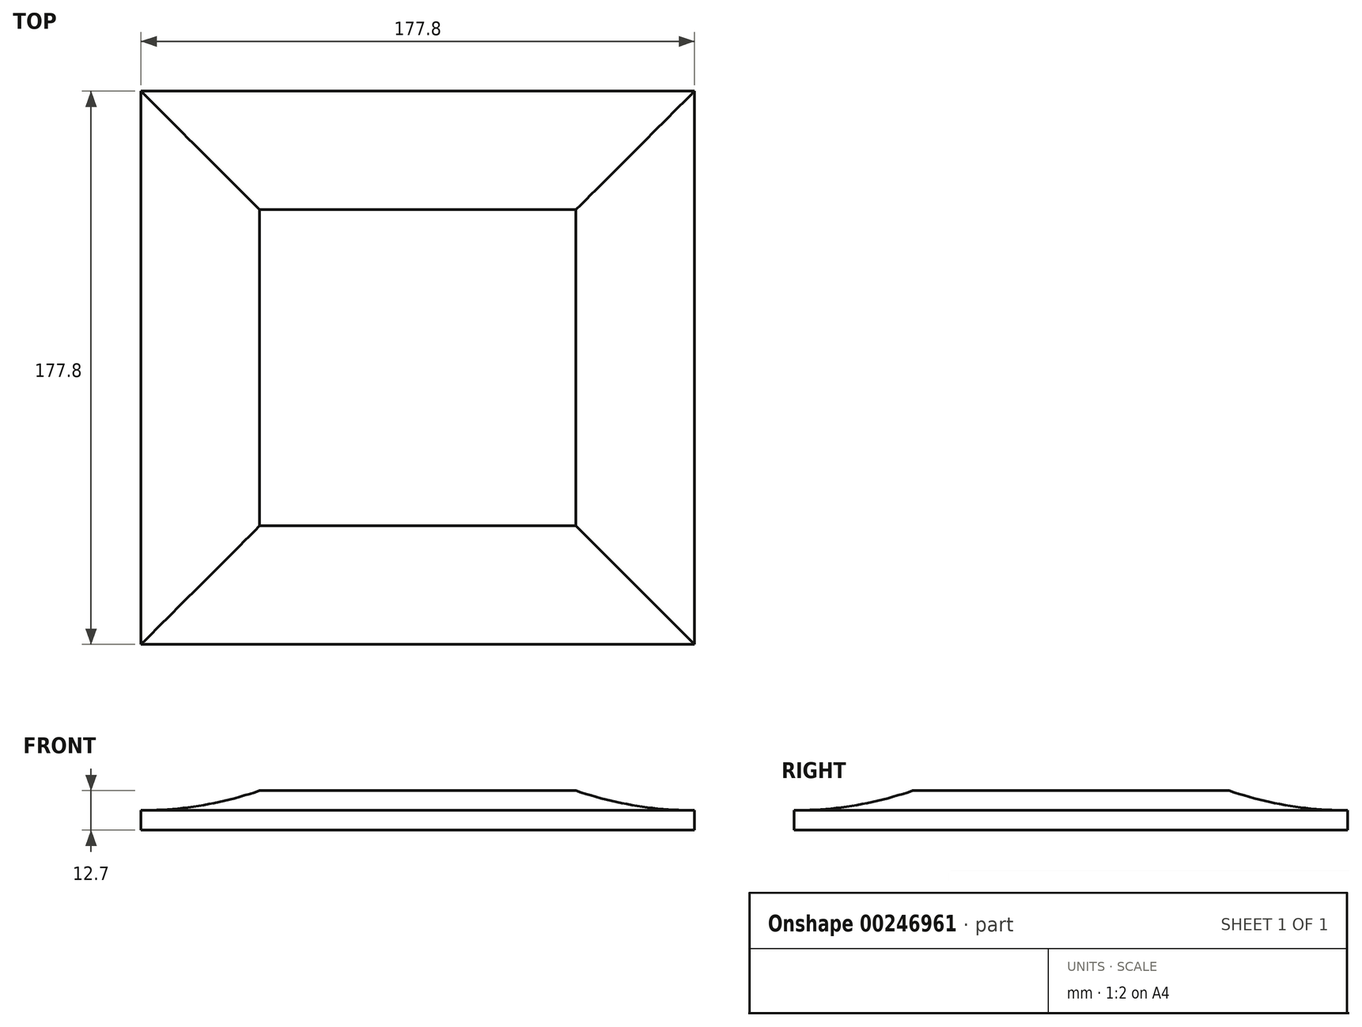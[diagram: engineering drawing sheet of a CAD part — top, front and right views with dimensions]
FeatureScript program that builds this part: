
annotation { "Feature Type Name" : "Feature", "Feature Type Description" : "" }
export const myFeature = defineFeature(function(context is Context, id is Id, definition is map)
    precondition{}
    {
        {
            var Q0;
            Q0=qCreatedBy(makeId("Top.planeOp"),FACE);
            var sketch = newSketch(context, id + "F0", { "sketchPlane" : qUnion([Q0])});
            skLineSegment(sketch, "E0.bottom", {"start": v(88.9, -88.9) * mm, "end": v(-88.9, -88.9) * mm});
            skLineSegment(sketch, "E0.top", {"start": v(88.9, 88.9) * mm, "end": v(-88.9, 88.9) * mm});
            skLineSegment(sketch, "E0.left", {"start": v(88.9, -88.9) * mm, "end": v(88.9, 88.9) * mm});
            skLineSegment(sketch, "E0.right", {"start": v(-88.9, -88.9) * mm, "end": v(-88.9, 88.9) * mm});
            skPoint(sketch, "E0.middle", {"position": v(0, 0) * mm});
            skSolve(sketch);
        }
        {
            var Q0;
            Q0=qCreatedBy(makeId("Front.planeOp"),FACE);
            var sketch = newSketch(context, id + "F1", { "sketchPlane" : qUnion([Q0])});
            skPoint(sketch, "E1.0", {"position": v(88.9, 0) * mm});
            skLineSegment(sketch, "E2", {"start": v(88.9, 0) * mm, "end": v(0, 0) * mm});
            skLineSegment(sketch, "E3", {"start": v(88.9, 0) * mm, "end": v(88.9, 6.35) * mm});
            skLineSegment(sketch, "E4", {"start": v(88.9, 6.35) * mm, "end": v(121.43, 6.35) * mm, "construction": true});
            skLineSegment(sketch, "E5", {"start": v(0, 0) * mm, "end": v(0, 12.7) * mm});
            skLineSegment(sketch, "E6", {"start": v(0, 12.7) * mm, "end": v(50.8, 12.7) * mm});
            skArc(sketch, "E7", {"start": v(88.9, 6.35) * mm, "mid": v(69.59, 7.95) * mm, "end": v(50.8, 12.7) * mm});
            skSolve(sketch);
        }
        {
            var Q0;
            Q0=makeQuery(id+"F1.imprint","IMPRINT",FACE,{"disambiguationData":[TD([[makeQuery(id+"F1.imprint","IMPRINT",EDGE,{"derivedFrom":sQuery(id+"F1.wireOp",EDGE,"E2")}),-1.0]])]});
            var Q1;
            Q1=sQuery(id+"F0.wireOp",EDGE,"E0.left");
            var Q2;
            Q2=sQuery(id+"F0.wireOp",EDGE,"E0.top");
            var Q3;
            Q3=sQuery(id+"F0.wireOp",EDGE,"E0.right");
            var Q4;
            Q4=sQuery(id+"F0.wireOp",EDGE,"E0.bottom");
            sweep(context, id + "F2", {"profiles" : qUnion([Q0]), "path" : qUnion([Q1, Q2, Q3, Q4])});
        }
    });
